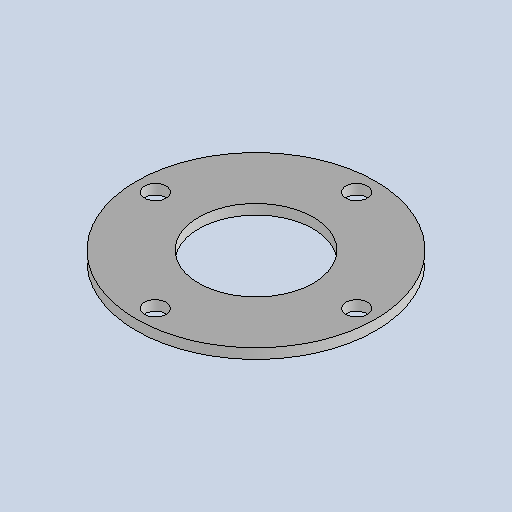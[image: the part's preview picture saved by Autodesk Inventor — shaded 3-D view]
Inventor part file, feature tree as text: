
AUTODESK INVENTOR PART (.ipt)
format: ipt  version: 2025.1 (Build 291241020, 241B)  size: 199,680 bytes
history: native  units: mm
features: other x3, sketch x2, sheet_metal_op x1, pattern_circular x1
ambient origin geometry x8: Origin, YZ Plane, XZ Plane, XY Plane, X Axis, Y Axis, Z Axis, Center Point
bodies: Body1 (feature_tree)
feature tree (7):
  sheet_metal_op  "Face2"
  pattern_circular  "Circular Pattern1"  [2 undecoded]
  sketch  "Sketch2"  dims[d14=8.0mm]
  other  "Plate2"
  sketch  "Sketch3"  dims[d15=17.0mm d17=8.0mm d18=0.0mm d19=40.0mm d20=360.0deg d25=91.0mm d27=190.0mm d28=160.0mm]
  other  "Cut1"
  other  "Definition1"
note: 2 required parameter values undecoded (feature->parameter linkage not recoverable at this tier; creation-order binding heuristic only, values carry confidence <= 0.55)
